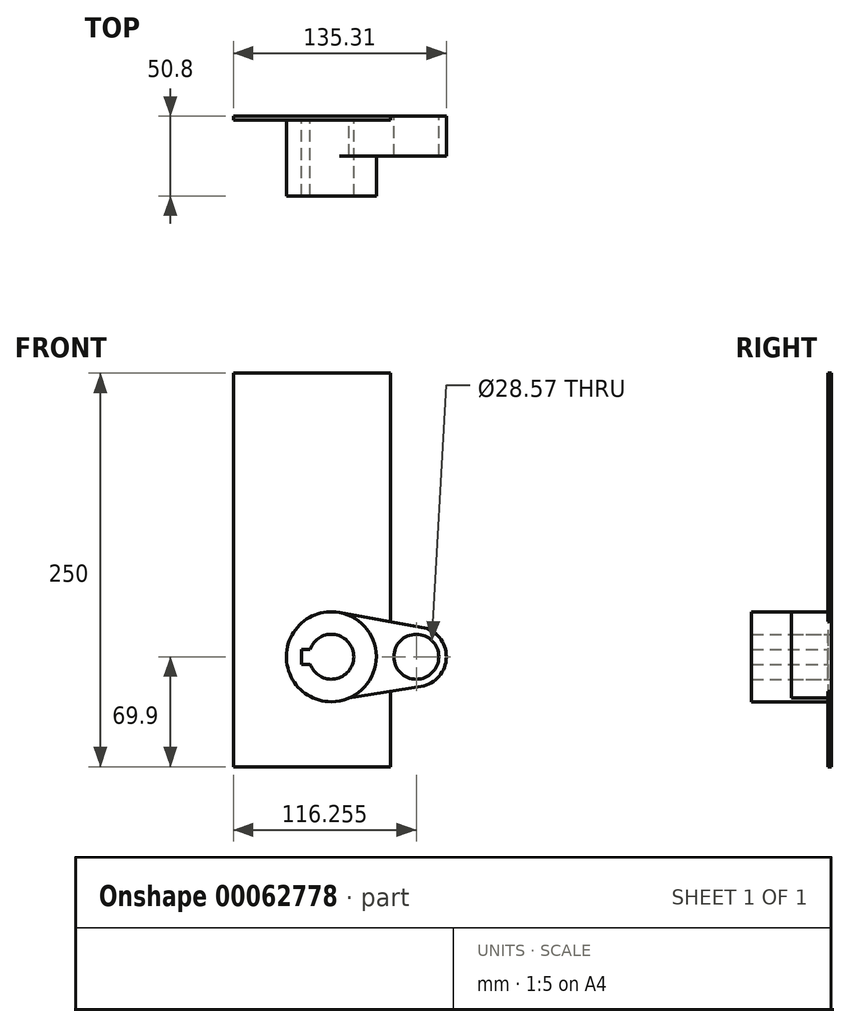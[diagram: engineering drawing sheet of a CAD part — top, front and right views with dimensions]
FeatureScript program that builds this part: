
annotation { "Feature Type Name" : "Feature", "Feature Type Description" : "" }
export const myFeature = defineFeature(function(context is Context, id is Id, definition is map)
    precondition{}
    {
        {
            var Q0;
            Q0=qCreatedBy(makeId("Front.planeOp"),FACE);
            var sketch = newSketch(context, id + "F0", { "sketchPlane" : qUnion([Q0])});
            skCircle(sketch, "E0", {"center": v(0, 0) * mm, "radius": 28.57 * mm});
            skCircle(sketch, "E1", {"center": v(53.98, 0) * mm, "radius": 19.05 * mm});
            skLineSegment(sketch, "E2", {"start": v(5.04, 28.13) * mm, "end": v(57.34, 18.75) * mm});
            skLineSegment(sketch, "E3", {"start": v(11.26, -26.26) * mm, "end": v(57.34, -18.75) * mm});
            skCircle(sketch, "E4", {"center": v(0, 0) * mm, "radius": 14.29 * mm});
            skCircle(sketch, "E5", {"center": v(53.98, 0) * mm, "radius": 14.29 * mm});
            skLineSegment(sketch, "E6.rect.bottom", {"start": v(-19.05, -4.76) * mm, "end": v(19.05, -4.76) * mm});
            skLineSegment(sketch, "E6.rect.top", {"start": v(-19.05, 4.76) * mm, "end": v(19.05, 4.76) * mm});
            skLineSegment(sketch, "E6.rect.left", {"start": v(-19.05, -4.76) * mm, "end": v(-19.05, 4.76) * mm});
            skLineSegment(sketch, "E6.rect.right", {"start": v(19.05, -4.76) * mm, "end": v(19.05, 4.76) * mm});
            skSolve(sketch);
        }
        {
            var Q0;
            {var subQ11=sQuery(id+"F0.wireOp",EDGE,"E6.rect.left");Q0=makeQuery(id+"F0.imprint","IMPRINT",FACE,{"disambiguationData":[TD([[makeQuery(id+"F0.imprint","IMPRINT",EDGE,{"derivedFrom":subQ11}),1.0]])]});}
            var Q1;
            {var subQ0=sQuery(id+"F0.wireOp",EDGE,"E2");Q1=makeQuery(id+"F0.imprint","IMPRINT",FACE,{"disambiguationData":[TD([[makeQuery(id+"F0.imprint","IMPRINT",EDGE,{"derivedFrom":subQ0}),-1.0]])]});}
            var Q2;
            Q2=makeQuery(id+"F0.imprint","IMPRINT",FACE,{"disambiguationData":[TD([[makeQuery(id+"F0.imprint","IMPRINT",EDGE,{"derivedFrom":sQuery(id+"F0.wireOp",EDGE,"E5")}),-1.0]])]});
            extrude(context, id + "F1", {"entities" : qUnion([Q0, Q1, Q2]), "depth" : 25.4 * mm});
        }
        {
            var Q0;
            {var subQ5=sQuery(id+"F0.wireOp",EDGE,"E6.rect.right");Q0=makeQuery(id+"F0.imprint","IMPRINT",FACE,{"disambiguationData":[TD([[makeQuery(id+"F0.imprint","IMPRINT",EDGE,{"derivedFrom":subQ5}),1.0]])]});}
            var Q1;
            {var subQ11=sQuery(id+"F0.wireOp",EDGE,"E6.rect.left");Q1=makeQuery(id+"F0.imprint","IMPRINT",FACE,{"disambiguationData":[TD([[makeQuery(id+"F0.imprint","IMPRINT",EDGE,{"derivedFrom":subQ11}),1.0]])]});}
            extrude(context, id + "F2", {"entities" : qUnion([Q0, Q1]), "operationType" : NewBodyOperationType.ADD, "depth" : 50.8 * mm});
        }
        {
            var Q0;
            Q0=qCreatedBy(makeId("Front.planeOp"),FACE);
            var sketch = newSketch(context, id + "F3", { "sketchPlane" : qUnion([Q0])});
            skLineSegment(sketch, "E7.bottom", {"start": v(-62.28, -69.9) * mm, "end": v(37.72, -69.9) * mm});
            skLineSegment(sketch, "E7.top", {"start": v(-62.28, 180.1) * mm, "end": v(37.72, 180.1) * mm});
            skLineSegment(sketch, "E7.left", {"start": v(-62.28, -69.9) * mm, "end": v(-62.28, 180.1) * mm});
            skLineSegment(sketch, "E7.right", {"start": v(37.72, -69.9) * mm, "end": v(37.72, 180.1) * mm});
            skSolve(sketch);
        }
        {
            var Q0;
            Q0 = qSketchRegion(id + "F3", true);
            extrude(context, id + "F4", {"entities" : qUnion([Q0]), "depth" : 2.5 * mm});
        }
        {
            var Q0;
            Q0 = qSketchRegion(id + "F3", true);
            extrude(context, id + "F5", {"entities" : qUnion([Q0]), "operationType" : NewBodyOperationType.ADD, "depth" : 2.5 * mm});
        }
    });
